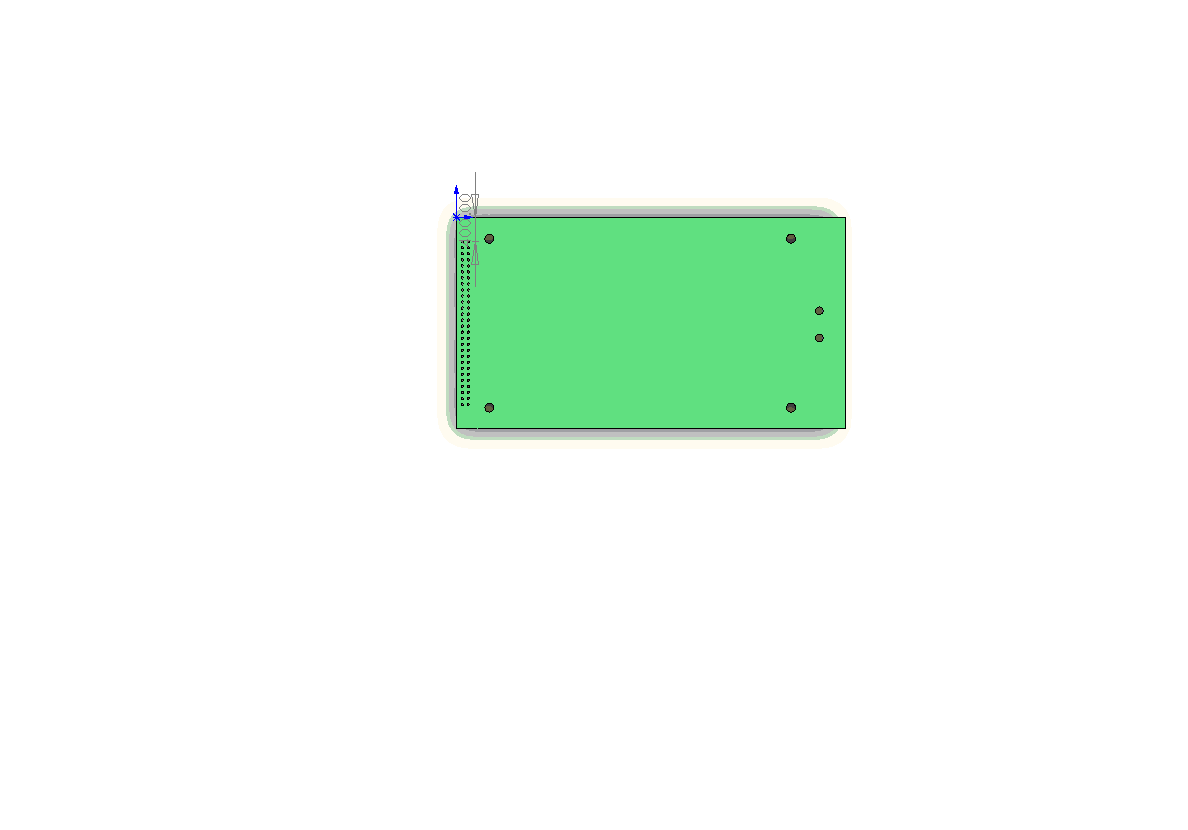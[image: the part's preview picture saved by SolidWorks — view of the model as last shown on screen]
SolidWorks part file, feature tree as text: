
SOLIDWORKS PART (.sldprt)
format: sldprt  version: not decoded by parser v0  size: 219,136 bytes
history: native  units: mm
features: sketch x4, cut_extrude x3, pattern_linear x2, material x1, extrude x1 + 1 further entry (+12 scaffold rows collapsed)
feature tree (24):
  "Annotations"  RD1=10.16mm
  scaffold x12  (default folders/planes/origin — collapsed)
  material  "Material <not specified>"
  sketch  "Sketch1"  dims[D1=163.83mm D2=88.9mm]
  extrude  "Extrude1"  Depth=1.5748mm
  sketch  "Sketch3"  dims[D1=3.2512mm D4=3.2512mm D2=38.227mm D3=10.922mm D5=11.43mm]
  cut_extrude  "Cut-Extrude2"  Depth=10mm
  sketch  "Sketch4"  dims[D1=3.81mm D4=3.81mm D7=3.81mm D8=3.81mm D2=8.89mm D3=13.97mm D5=8.89mm D6=13.97mm D9=8.89mm D10=8.89mm D11=8.89mm D12=8.89mm]
  cut_extrude  "Mount Holes"  Depth=10mm
  pattern_linear  "Mount Hole Pattern"  Count1=2 Count2=2 Spacing1=71.12mm Spacing2=127mm
  sketch  "Mount pin holes"  dims[D1=1.04mm D2=10.16mm D3=2.54mm]
  cut_extrude  "Connector Pin 1"  Depth=2.54mm
  pattern_linear  "LPattern1"  Count1=28 Count2=2 Spacing1=2.54mm Spacing2=2.54mm
decode coverage: 10 of 10 modeling features carry decoded parameters; 1 rows unclassified (native names shown)
note: suppression state not decoded; provenance and decode notes live in map.json
